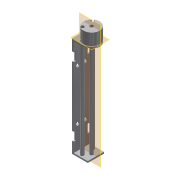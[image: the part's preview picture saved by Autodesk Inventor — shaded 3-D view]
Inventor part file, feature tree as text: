
AUTODESK INVENTOR PART (.ipt)
format: ipt  version: 2022 (Build 260153000, 153)  size: 198,144 bytes
history: native  units: mm
features: extrude x5, sketch x5, projected_geometry x5, plane x2, mirror x1
ambient origin geometry x8: Origin, YZ Plane, XZ Plane, XY Plane, X Axis, Y Axis, Z Axis, Center Point
bodies: Volumenkörper1 (feature_tree)
feature tree (18):
  extrude  "Extrusion1"  Depth=15.1mm
  mirror  "Spiegeln1"
  extrude  "Extrusion2"  Depth=3.14mm
  extrude  "Extrusion3"  Depth=23.0mm
  plane  "Arbeitsebene1"
  extrude  "Extrusion4"  Depth=4.0mm
  extrude  "Extrusion5"  Depth=2.0mm
  plane  "Work Plane2"
  sketch  "Skizze1"  dims[d0=92.9mm d1=15.1mm]
  sketch  "Skizze2"  dims[d2=3.14mm d3=3.14mm]
  projected_geometry  "Projizierte Kontur1"
  sketch  "Skizze3"  dims[d4=23.0mm d5=23.0mm]
  projected_geometry  "Projizierte Kontur2"
  projected_geometry  "Projizierte Kontur3"
  sketch  "Skizze4"  dims[d6=4.0mm d7=4.0mm]
  projected_geometry  "Projizierte Kontur4"
  sketch  "Skizze5"  dims[d8=8.0mm d9=2.0mm d10=10.5mm d11=2.0mm d12=1.4mm d13=0.0mm d14=3.0mm d15=10.5mm d16=3.1mm d17=3.1mm d18=6.75mm d19=6.75mm d20=2.64mm d21=2.64mm d22=13.11mm d23=1.44mm d24=0.0mm d25=1.44mm d26=0.0mm d27=0.5mm d28=14.95mm d29=10.86mm d30=0.0mm d31=10.86mm d32=0.0mm]
  projected_geometry  "Projizierte Kontur5"
